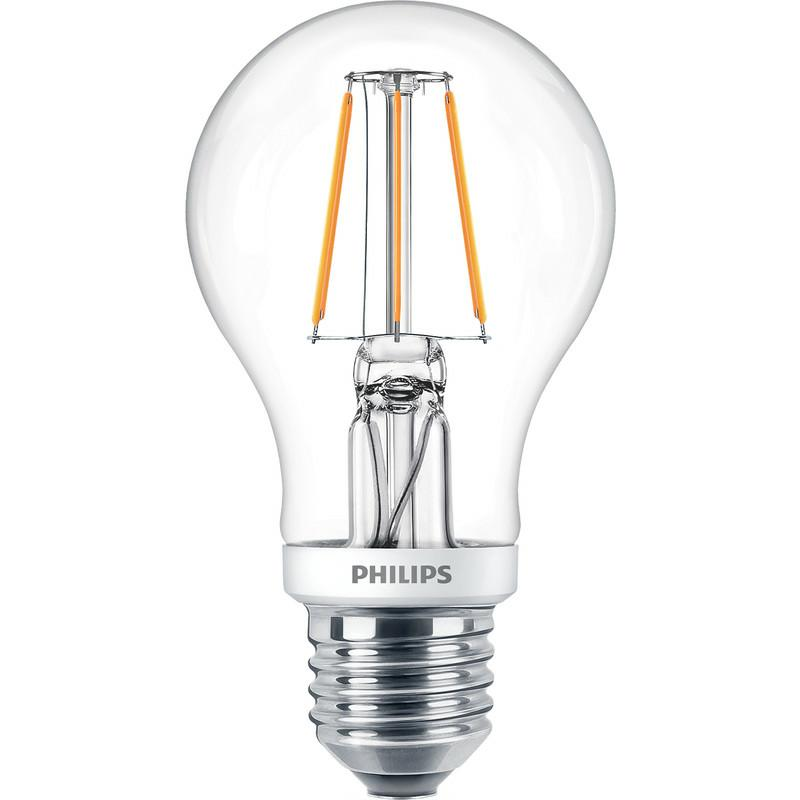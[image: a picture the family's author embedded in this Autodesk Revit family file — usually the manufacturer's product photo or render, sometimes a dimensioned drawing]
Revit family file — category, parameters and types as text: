
# Revit family: 63_UN_Pendant_RD Series Apple_Signify
name_source: partatom
category: Lighting Fixtures
units: mm (PartAtom-declared; Revit-internal decimal feet)

## family parameters
Always vertical = Yes
Cut with Voids When Loaded = Yes
Light Source = No
OmniClass Number = 23.80.70.11.14.11
OmniClass Title = Downlights
Part Type = Normal
Room Calculation Point = Yes
Round Connector Dimension = Use Diameter
Shared = No
Work Plane-Based = No

## types (1)
- Material defines types
    Apparent Load = 19 VA
    Assembly Code = 63.0
    Housing_Material = Select RGB Value for different appearance
    IfcExportAs = IfcLightFixtureType
    IfcExportType = USERDEFINED
    Lamp = LED
    Light Source = RD Series Apple - Lightsource : -
    Manufacturer = Signify
    Model = Decorative Pendants RD Series
    Pendant_Material = Select RGB Value for different appearance
    Type Comments = RD Series
    URL = https://www.signify.com
    Voltage = 230 V
    Wattage Comments = 19 W

## geometry (parser evidence)
native form markers: Sweep x9
no freeform markers — native parametric forms only
